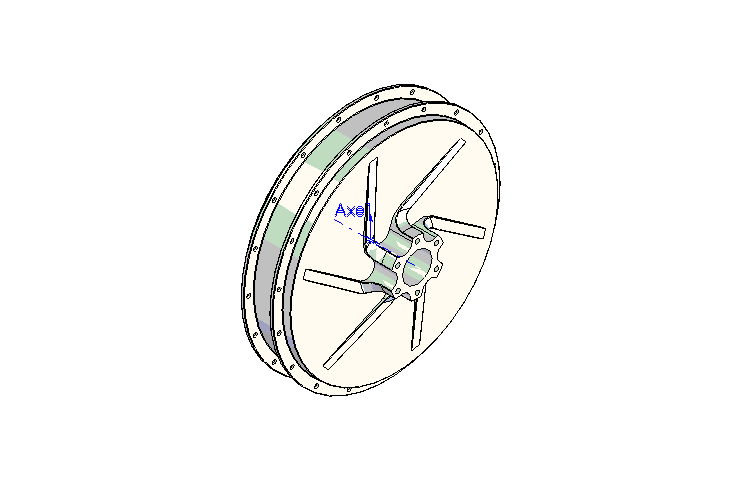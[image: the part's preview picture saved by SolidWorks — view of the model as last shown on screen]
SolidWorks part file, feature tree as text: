
SOLIDWORKS PART (.sldprt)
format: sldprt  version: not decoded by parser v0  size: 1,537,024 bytes
history: native  units: mm
features: sketch x8, cut_extrude x5, plane x3, fillet x2, pattern_circular x2, material x1, revolve x1, chamfer x1, extrude x1, cut_revolve x1, mirror x1 (+10 scaffold rows collapsed)
feature tree (36):
  scaffold x10  (default folders/planes/origin — collapsed)
  material  "Matériau <non spécifié>"
  plane  "Plan de face"
  plane  "Plan de dessus"
  plane  "Plan de droite"
  sketch  "Esquisse1"  dims[D1=32.0mm D2=26.0mm D3=48.0mm D4=230.0mm D5=210.0mm]
  revolve  "Révolution1"  Angle=360deg
  fillet  "Congé1"  Radius=0.5mm
  sketch  "Esquisse2"  dims[D1=2.0mm D2=220.0mm]
  cut_extrude  "Enlèv. mat.-Extru.1"  [1 undecoded]
  sketch  "Esquisse3"  dims[c1.D1=~126.876347mm c2.D1=10.0deg]
  cut_extrude  "Enlèv. mat.-Extru.2"  [1 undecoded]
  chamfer  "Chanfrein1"  Distance=1mm Angle=45deg
  pattern_circular  "Répétition circulaire1"  Count=18 Angle=20deg
  sketch  "Esquisse5"  dims[D1=190.0mm D2=30.0mm]
  extrude  "Extrusion1"  Depth=47mm
  sketch  "Esquisse6"  dims[c1.D1=9.0mm c1.D2=40.0mm c1.D3=20.0mm c1.D4=87.0mm c1.D5=~64.699845mm c2.D5=60.0deg c2.D6=25.0mm c2.D7=~67.213754mm c3.D7=5.0deg]
  cut_extrude  "Enlèv. mat.-Extru.3"  [1 undecoded]
  sketch  "Esquisse8"  dims[D1=4.5mm D2=45.0mm]
  cut_extrude  "Enlèv. mat.-Extru.4"  Depth=25mm
  pattern_circular  "Répétition circulaire2"  Count=6 Angle=60deg
  sketch  "Esquisse7"  dims[D1=10.0mm D2=55.0mm D3=190.0mm D4=3.0mm]
  cut_revolve  "Enlèvement de matière-Révolution1"  Angle=360deg
  fillet  "Congé2"  Radius=0.5mm
  mirror  "Symétrie3"
  sketch  "Esquisse9"  dims[D1=20.0mm]
  cut_extrude  "Enlèv. mat.-Extru.5"  [1 undecoded]
decode coverage: 17 of 22 modeling features carry decoded parameters
note: ~ marks probable driven/reference dimensions
note: 4 parameter values undecoded
summary: no parameter record found for 4 features
note: suppression state not decoded; provenance and decode notes live in map.json
